# Revit family: BOX BV
name_source: partatom
category: Modelos genéricos
revit_build: Autodesk Revit 2017 (Build: 20160225_1515(x64)
units: mm (PartAtom-declared; Revit-internal decimal feet)

## family parameters
Compartido = No
Corte con vacíos al cargar = No
Cota de conector redondo = Diámetro de uso
Puede alojar armadura = No
Punto de cálculo de habitación = No
Se basa en plano de trabajo = No
Siempre vertical = Sí
Tipo de pieza = Normal

## types (6) — shared parameters
Esp = 3 mm  [stored 0.00984252 ft]
Fabricante = Casals Ventilación
M = 23 mm  [stored 0.0754593 ft]
Material = <Por categoría>
N = 27 mm  [stored 0.0885827 ft]
URL = www.casals.com

## per-type parameters (varying)
| type | A | B | C | D | Dimensiones | E | F | H | I | J | K | L |
| BOX BV 7/7 | 450 mm  [stored 1.47638 ft] | 450 mm  [stored 1.47638 ft] | 698 mm | 242 mm  [stored 0.793963 ft] | 450x450x748 | 218 mm | 81 mm  [stored 0.265748 ft] | 151 mm  [stored 0.495407 ft] | 352 mm  [stored 1.15486 ft] | 311 mm  [stored 1.02034 ft] | 60 mm  [stored 0.19685 ft] | 79 mm |
| BOX BV 9/9 | 535 mm | 535 mm | 768 mm | 311 mm  [stored 1.02034 ft] | 535x535x818 | 270 mm | 96 mm  [stored 0.314961 ft] | 169 mm  [stored 0.554462 ft] | 418 mm  [stored 1.37139 ft] | 361 mm | 78 mm  [stored 0.255906 ft] | 96 mm  [stored 0.314961 ft] |
| BOX BV 10/10 | 580 mm | 580 mm | 798 mm | 342 mm  [stored 1.12205 ft] | 580x580x848 | 301 mm  [stored 0.987533 ft] | 84 mm  [stored 0.275591 ft] | 195 mm  [stored 0.639764 ft] | 493 mm | 423 mm | 69 mm  [stored 0.226378 ft] | 88 mm  [stored 0.288714 ft] |
| BOX BV 12/12 | 650 mm | 650 mm | 868 mm | 408 mm | 650x650x918 | 351 mm | 83 mm  [stored 0.27231 ft] | 216 mm  [stored 0.708661 ft] | 576 mm | 502 mm | 65 mm  [stored 0.213255 ft] | 83 mm  [stored 0.27231 ft] |
| BOX BV 15/15 | 775 mm | 775 mm | 988 mm | 483 mm | 775x775x1038 | 413 mm | 118 mm | 244 mm  [stored 0.800525 ft] | 650 mm | 652 mm | 52 mm | 71 mm  [stored 0.23294 ft] |
| BOX BV 18/18 | 870 mm | 885 mm | 1168 mm | 566 mm | 870x885x1218
870x885x1218 | 491 mm | 104 mm | 290 mm  [stored 0.951444 ft] | 750 mm | 752 mm | 57 mm  [stored 0.187008 ft] | 76 mm  [stored 0.249344 ft] |

note: [stored X ft] marks values corroborated as IEEE doubles in the binary element streams (Revit-internal decimal feet)
